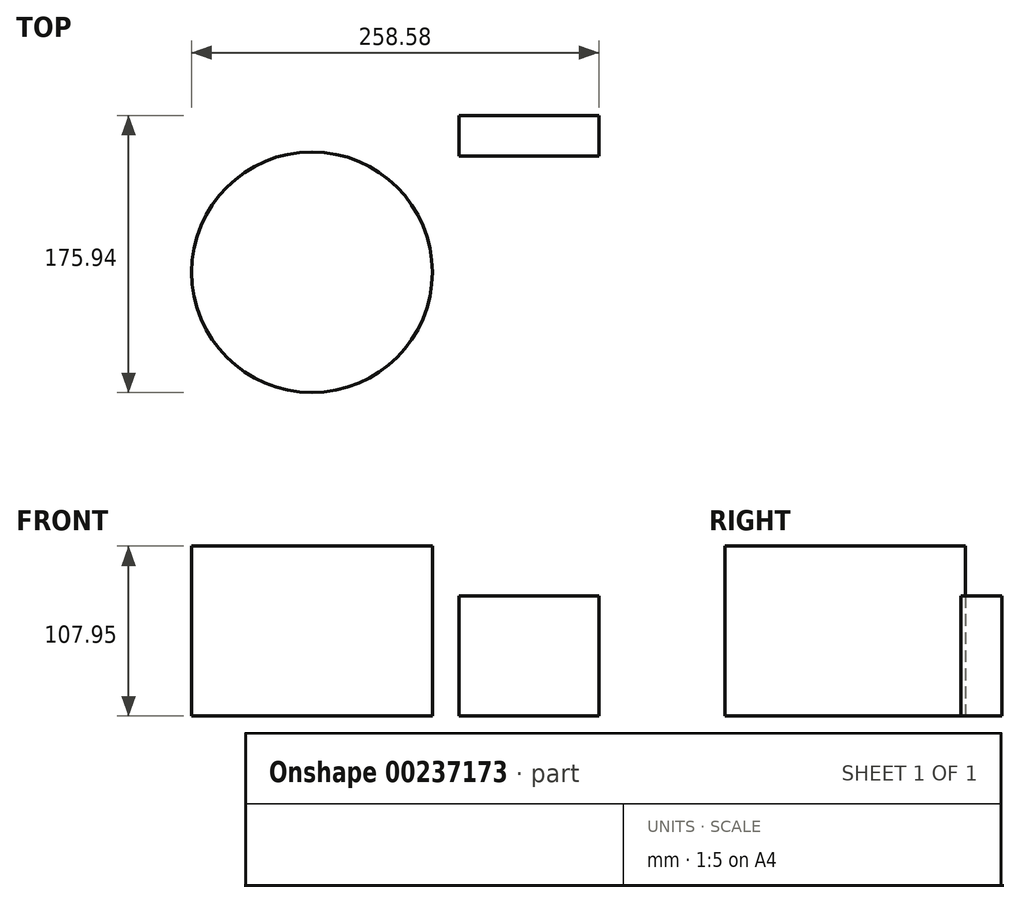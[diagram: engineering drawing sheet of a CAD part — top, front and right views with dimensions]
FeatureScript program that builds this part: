
annotation { "Feature Type Name" : "Feature", "Feature Type Description" : "" }
export const myFeature = defineFeature(function(context is Context, id is Id, definition is map)
    precondition{}
    {
        {
            var Q0;
            Q0=qCreatedBy(makeId("Top.planeOp"),FACE);
            var sketch = newSketch(context, id + "F0", { "sketchPlane" : qUnion([Q0])});
            skCircle(sketch, "E0", {"center": v(-46.33, -38.92) * mm, "radius": 76.42 * mm});
            skLineSegment(sketch, "E1.bottom", {"start": v(33.28, 48.39) * mm, "end": v(123.04, 48.39) * mm});
            skLineSegment(sketch, "E1.top", {"start": v(33.28, 22.96) * mm, "end": v(123.04, 22.96) * mm});
            skLineSegment(sketch, "E1.left", {"start": v(33.28, 48.39) * mm, "end": v(33.28, 22.96) * mm});
            skLineSegment(sketch, "E1.right", {"start": v(123.04, 48.39) * mm, "end": v(123.04, 22.96) * mm});
            skSolve(sketch);
        }
        {
            var Q0;
            Q0=makeQuery(id+"F0.imprint","IMPRINT",FACE,{"disambiguationData":[TD([[makeQuery(id+"F0.imprint","IMPRINT",EDGE,{"derivedFrom":sQuery(id+"F0.wireOp",EDGE,"E0")}),1.0]])]});
            extrude(context, id + "F1", {"entities" : qUnion([Q0]), "depth" : 107.95 * mm});
        }
        {
            var Q0;
            Q0=qCreatedBy(makeId("Top.planeOp"),FACE);
            var sketch = newSketch(context, id + "F2", { "sketchPlane" : qUnion([Q0])});
            skLineSegment(sketch, "E2.bottom", {"start": v(46.9, 60.6) * mm, "end": v(135.84, 60.6) * mm});
            skLineSegment(sketch, "E2.top", {"start": v(46.9, 34.7) * mm, "end": v(135.84, 34.7) * mm});
            skLineSegment(sketch, "E2.left", {"start": v(46.9, 60.6) * mm, "end": v(46.9, 34.7) * mm});
            skLineSegment(sketch, "E2.right", {"start": v(135.84, 60.6) * mm, "end": v(135.84, 34.7) * mm});
            skSolve(sketch);
        }
        {
            var Q0;
            Q0=makeQuery(id+"F2.imprint","IMPRINT",FACE,{"disambiguationData":[TD([[makeQuery(id+"F2.imprint","IMPRINT",EDGE,{"derivedFrom":sQuery(id+"F2.wireOp",EDGE,"E2.bottom")}),-1.0]])]});
            extrude(context, id + "F3", {"entities" : qUnion([Q0]), "depth" : 76.2 * mm});
        }
    });
